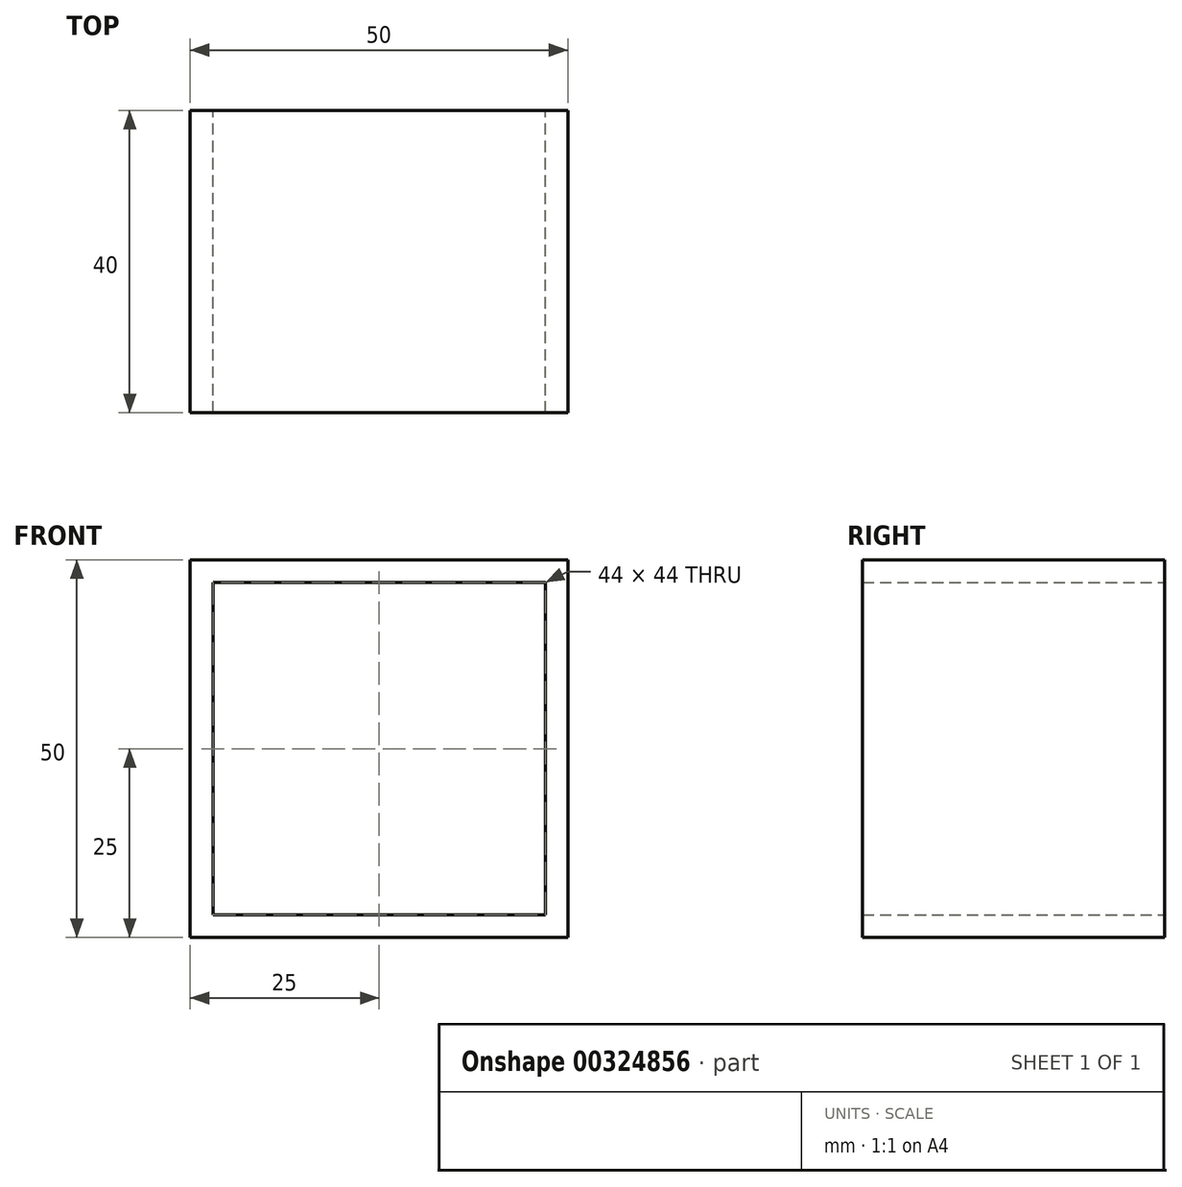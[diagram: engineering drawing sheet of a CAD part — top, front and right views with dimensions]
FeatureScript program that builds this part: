
annotation { "Feature Type Name" : "Feature", "Feature Type Description" : "" }
export const myFeature = defineFeature(function(context is Context, id is Id, definition is map)
    precondition{}
    {
        {
            var Q0;
            Q0=qCreatedBy(makeId("Front.planeOp"),FACE);
            var sketch = newSketch(context, id + "F0", { "sketchPlane" : qUnion([Q0])});
            skLineSegment(sketch, "E0.bottom", {"start": v(-25, 25) * mm, "end": v(25, 25) * mm});
            skLineSegment(sketch, "E0.top", {"start": v(-25, -25) * mm, "end": v(25, -25) * mm});
            skLineSegment(sketch, "E0.left", {"start": v(-25, 25) * mm, "end": v(-25, -25) * mm});
            skLineSegment(sketch, "E0.right", {"start": v(25, 25) * mm, "end": v(25, -25) * mm});
            skPoint(sketch, "E0.middle", {"position": v(0, 0) * mm});
            skLineSegment(sketch, "E1.bottom", {"start": v(-22, 22) * mm, "end": v(22, 22) * mm});
            skLineSegment(sketch, "E1.top", {"start": v(-22, -22) * mm, "end": v(22, -22) * mm});
            skLineSegment(sketch, "E1.left", {"start": v(-22, 22) * mm, "end": v(-22, -22) * mm});
            skLineSegment(sketch, "E1.right", {"start": v(22, 22) * mm, "end": v(22, -22) * mm});
            skSolve(sketch);
        }
        {
            var Q0;
            Q0=makeQuery(id+"F0.imprint","IMPRINT",FACE,{"disambiguationData":[TD([[makeQuery(id+"F0.imprint","IMPRINT",EDGE,{"derivedFrom":sQuery(id+"F0.wireOp",EDGE,"E0.bottom")}),-1.0]])]});
            extrude(context, id + "F1", {"entities" : qUnion([Q0]), "depth" : 40 * mm, "symmetric" : true});
        }
    });
